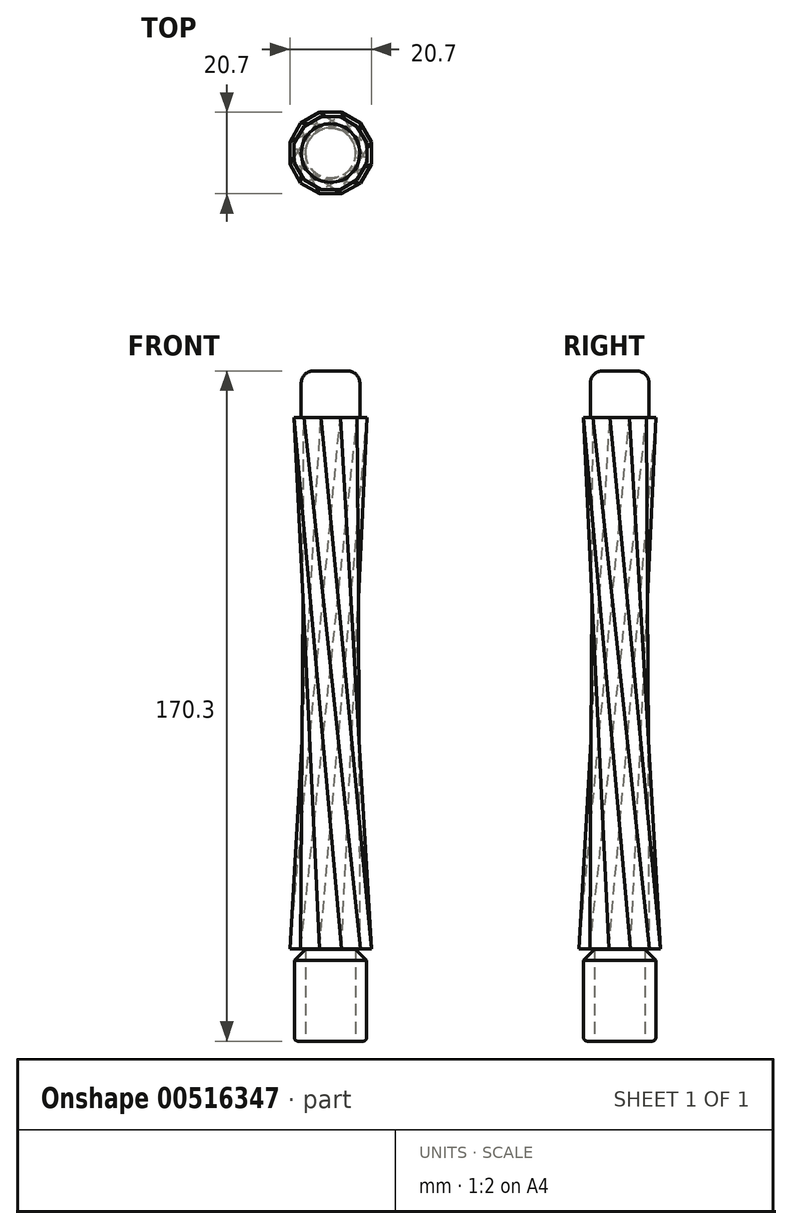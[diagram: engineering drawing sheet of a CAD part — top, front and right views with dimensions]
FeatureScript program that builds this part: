
annotation { "Feature Type Name" : "Feature", "Feature Type Description" : "" }
export const myFeature = defineFeature(function(context is Context, id is Id, definition is map)
    precondition{}
    {
        {
            var Q0;
            Q0=qCreatedBy(makeId("Top.planeOp"),FACE);
            cPlane(context, id + "F0", {"entities" : qUnion([Q0]), "cplaneType" : CPlaneType.OFFSET, "offset" : 2.5 * mm, "oppositeDirection" : true, "width" : 150 * mm, "height" : 150 * mm});
        }
        {
            var Q0;
            Q0=qCreatedBy(id+"F0.planeOp",FACE);
            var sketch = newSketch(context, id + "F1", { "sketchPlane" : qUnion([Q0])});
            skCircle(sketch, "E0", {"center": v(0, 0) * mm, "radius": 6.4 * mm});
            skCircle(sketch, "E1", {"center": v(0, 0) * mm, "radius": 9.2 * mm});
            skCircle(sketch, "E2", {"center": v(0, 0) * mm, "radius": 10.35 * mm});
            skSolve(sketch);
        }
        {
            var Q0;
            Q0=qCreatedBy(makeId("Top.planeOp"),FACE);
            cPlane(context, id + "F2", {"entities" : qUnion([Q0]), "cplaneType" : CPlaneType.OFFSET, "offset" : 21 * mm, "width" : 150 * mm, "height" : 150 * mm});
        }
        {
            var Q0;
            Q0=qCreatedBy(id+"F2.planeOp",FACE);
            var sketch = newSketch(context, id + "F3", { "sketchPlane" : qUnion([Q0])});
            skCircle(sketch, "E3", {"center": v(0, 0) * mm, "radius": 6.4 * mm});
            skCircle(sketch, "E4", {"center": v(0, 0) * mm, "radius": 9.2 * mm});
            skCircle(sketch, "E5", {"center": v(0, 0) * mm, "radius": 10.35 * mm});
            skSolve(sketch);
        }
        {
            var Q0;
            Q0=qCreatedBy(id+"F2.planeOp",FACE);
            cPlane(context, id + "F4", {"entities" : qUnion([Q0]), "cplaneType" : CPlaneType.OFFSET, "offset" : 135 * mm, "width" : 150 * mm, "height" : 150 * mm});
        }
        {
            var Q0;
            Q0=qCreatedBy(id+"F4.planeOp",FACE);
            var sketch = newSketch(context, id + "F5", { "sketchPlane" : qUnion([Q0])});
            skPoint(sketch, "E6.0", {"position": v(0, 0) * mm});
            skCircle(sketch, "E7", {"center": v(0, 0) * mm, "radius": 4.9 * mm});
            skCircle(sketch, "E8", {"center": v(0, 0) * mm, "radius": 7.45 * mm});
            skCircle(sketch, "E9", {"center": v(0, 0) * mm, "radius": 9.25 * mm});
            skSolve(sketch);
        }
        {
            var Q0;
            Q0=qCreatedBy(id+"F4.planeOp",FACE);
            cPlane(context, id + "F6", {"entities" : qUnion([Q0]), "cplaneType" : CPlaneType.OFFSET, "offset" : 11.8 * mm, "width" : 150 * mm, "height" : 150 * mm});
        }
        {
            var Q0;
            Q0=qCreatedBy(id+"F6.planeOp",FACE);
            var sketch = newSketch(context, id + "F7", { "sketchPlane" : qUnion([Q0])});
            skPoint(sketch, "E10.0", {"position": v(0, 0) * mm});
            skCircle(sketch, "E11", {"center": v(0, 0) * mm, "radius": 4.9 * mm});
            skCircle(sketch, "E12", {"center": v(0, 0) * mm, "radius": 7.45 * mm});
            skCircle(sketch, "E13", {"center": v(0, 0) * mm, "radius": 9.25 * mm});
            skSolve(sketch);
        }
        {
            var Q0;
            Q0=qCreatedBy(makeId("Front.planeOp"),FACE);
            var sketch = newSketch(context, id + "F8", { "sketchPlane" : qUnion([Q0])});
            skPoint(sketch, "E14.0", {"position": v(0, 167.8) * mm});
            skLineSegment(sketch, "E15", {"start": v(0, 167.8) * mm, "end": v(0, 0) * mm, "construction": true});
            skCircle(sketch, "E16", {"center": v(0, 36.85) * mm, "radius": 2.35 * mm});
            skCircle(sketch, "E17", {"center": v(0, 57.2) * mm, "radius": 2.6 * mm});
            skCircle(sketch, "E18", {"center": v(0, 79.25) * mm, "radius": 2.75 * mm});
            skCircle(sketch, "E19", {"center": v(0, 102.2) * mm, "radius": 2.3 * mm});
            skCircle(sketch, "E20", {"center": v(0, 127.6) * mm, "radius": 3 * mm});
            skCircle(sketch, "E21", {"center": v(2.3, 147.6) * mm, "radius": 2.1 * mm});
            skCircle(sketch, "E22", {"center": v(-3.01, 148.25) * mm, "radius": 1.45 * mm});
            skCircle(sketch, "E23", {"center": v(0, 30.75) * mm, "radius": 2.75 * mm});
            skSolve(sketch);
        }
        {
            var Q0;
            Q0=makeQuery(id+"F1.imprint","IMPRINT",FACE,{"disambiguationData":[TD([[makeQuery(id+"F1.imprint","IMPRINT",EDGE,{"derivedFrom":sQuery(id+"F1.wireOp",EDGE,"E0")}),1.0]])]});
            var Q1;
            Q1=makeQuery(id+"F3.imprint","IMPRINT",FACE,{"disambiguationData":[TD([[makeQuery(id+"F3.imprint","IMPRINT",EDGE,{"derivedFrom":sQuery(id+"F3.wireOp",EDGE,"E3")}),1.0]])]});
            var Q2;
            Q2=makeQuery(id+"F5.imprint","IMPRINT",FACE,{"disambiguationData":[TD([[makeQuery(id+"F5.imprint","IMPRINT",EDGE,{"derivedFrom":sQuery(id+"F5.wireOp",EDGE,"E7")}),1.0]])]});
            var Q3;
            Q3=makeQuery(id+"F7.imprint","IMPRINT",FACE,{"disambiguationData":[TD([[makeQuery(id+"F7.imprint","IMPRINT",EDGE,{"derivedFrom":sQuery(id+"F7.wireOp",EDGE,"E11")}),1.0]])]});
            loft(context, id + "F9", {"sheetProfilesArray" : [{ "sheetProfileEntities" : qUnion([Q0]) }, { "sheetProfileEntities" : qUnion([Q1]) }, { "sheetProfileEntities" : qUnion([Q2]) }, { "sheetProfileEntities" : qUnion([Q3]) }]});
        }
        {
            var Q0;
            Q0=makeQuery(id+"F8.imprint","IMPRINT",FACE,{"disambiguationData":[TD([[makeQuery(id+"F8.imprint","IMPRINT",EDGE,{"derivedFrom":sQuery(id+"F8.wireOp",EDGE,"E23")}),1.0]])]});
            extrude(context, id + "F10", {"entities" : qUnion([Q0]), "operationType" : NewBodyOperationType.ADD, "oppositeDirection" : true, "depth" : 15 * mm});
        }
        {
            var Q0;
            Q0=makeQuery(id+"F8.imprint","IMPRINT",FACE,{"disambiguationData":[TD([[makeQuery(id+"F8.imprint","IMPRINT",EDGE,{"derivedFrom":sQuery(id+"F8.wireOp",EDGE,"E16")}),1.0]])]});
            var Q1;
            Q1=makeQuery(id+"F8.imprint","IMPRINT",FACE,{"disambiguationData":[TD([[makeQuery(id+"F8.imprint","IMPRINT",EDGE,{"derivedFrom":sQuery(id+"F8.wireOp",EDGE,"E17")}),1.0]])]});
            var Q2;
            Q2=makeQuery(id+"F8.imprint","IMPRINT",FACE,{"disambiguationData":[TD([[makeQuery(id+"F8.imprint","IMPRINT",EDGE,{"derivedFrom":sQuery(id+"F8.wireOp",EDGE,"E18")}),1.0]])]});
            var Q3;
            Q3=makeQuery(id+"F8.imprint","IMPRINT",FACE,{"disambiguationData":[TD([[makeQuery(id+"F8.imprint","IMPRINT",EDGE,{"derivedFrom":sQuery(id+"F8.wireOp",EDGE,"E19")}),1.0]])]});
            var Q4;
            Q4=makeQuery(id+"F8.imprint","IMPRINT",FACE,{"disambiguationData":[TD([[makeQuery(id+"F8.imprint","IMPRINT",EDGE,{"derivedFrom":sQuery(id+"F8.wireOp",EDGE,"E20")}),1.0]])]});
            var Q5;
            Q5=makeQuery(id+"F8.imprint","IMPRINT",FACE,{"disambiguationData":[TD([[makeQuery(id+"F8.imprint","IMPRINT",EDGE,{"derivedFrom":sQuery(id+"F8.wireOp",EDGE,"E21")}),1.0]])]});
            var Q6;
            Q6=makeQuery(id+"F8.imprint","IMPRINT",FACE,{"disambiguationData":[TD([[makeQuery(id+"F8.imprint","IMPRINT",EDGE,{"derivedFrom":sQuery(id+"F8.wireOp",EDGE,"E22")}),1.0]])]});
            extrude(context, id + "F11", {"entities" : qUnion([Q0, Q1, Q2, Q3, Q4, Q5, Q6]), "operationType" : NewBodyOperationType.ADD, "depth" : 15 * mm});
        }
        {
            var Q0;
            Q0=makeQuery(id+"F1.imprint","IMPRINT",FACE,{"disambiguationData":[TD([[makeQuery(id+"F1.imprint","IMPRINT",EDGE,{"derivedFrom":sQuery(id+"F1.wireOp",EDGE,"E0")}),-1.0]])]});
            var Q1;
            Q1=makeQuery(id+"F1.imprint","IMPRINT",FACE,{"disambiguationData":[TD([[makeQuery(id+"F1.imprint","IMPRINT",EDGE,{"derivedFrom":sQuery(id+"F1.wireOp",EDGE,"E0")}),1.0]])]});
            extrude(context, id + "F12", {"entities" : qUnion([Q0, Q1]), "depth" : 23.5 * mm, "offsetDistance" : 25 * mm});
        }
        {
            var Q0;
            Q0=makeQuery(id+"F7.imprint","IMPRINT",FACE,{"disambiguationData":[TD([[makeQuery(id+"F7.imprint","IMPRINT",EDGE,{"derivedFrom":sQuery(id+"F7.wireOp",EDGE,"E11")}),-1.0]])]});
            var Q1;
            Q1=makeQuery(id+"F7.imprint","IMPRINT",FACE,{"disambiguationData":[TD([[makeQuery(id+"F7.imprint","IMPRINT",EDGE,{"derivedFrom":sQuery(id+"F7.wireOp",EDGE,"E11")}),1.0]])]});
            extrude(context, id + "F13", {"entities" : qUnion([Q0, Q1]), "oppositeDirection" : true, "depth" : 11.8 * mm, "offsetDistance" : 25 * mm});
        }
        {
            var Q0;
            Q0=qCreatedBy(id+"F2.planeOp",FACE);
            var sketch = newSketch(context, id + "F14", { "sketchPlane" : qUnion([Q0])});
            skPoint(sketch, "E24.0", {"position": v(0, 0) * mm});
            skLineSegment(sketch, "E25.0", {"start": v(-2.77, 10.35) * mm, "end": v(2.77, 10.35) * mm});
            skLineSegment(sketch, "E25.1", {"start": v(2.77, 10.35) * mm, "end": v(7.58, 7.58) * mm});
            skLineSegment(sketch, "E25.2", {"start": v(7.58, 7.58) * mm, "end": v(10.35, 2.77) * mm});
            skLineSegment(sketch, "E25.3", {"start": v(10.35, 2.77) * mm, "end": v(10.35, -2.77) * mm});
            skLineSegment(sketch, "E25.4", {"start": v(10.35, -2.77) * mm, "end": v(7.58, -7.58) * mm});
            skLineSegment(sketch, "E25.5", {"start": v(7.58, -7.58) * mm, "end": v(2.77, -10.35) * mm});
            skLineSegment(sketch, "E25.6", {"start": v(2.77, -10.35) * mm, "end": v(-2.77, -10.35) * mm});
            skLineSegment(sketch, "E25.7", {"start": v(-2.77, -10.35) * mm, "end": v(-7.58, -7.58) * mm});
            skLineSegment(sketch, "E25.8", {"start": v(-7.58, -7.58) * mm, "end": v(-10.35, -2.77) * mm});
            skLineSegment(sketch, "E25.9", {"start": v(-10.35, -2.77) * mm, "end": v(-10.35, 2.77) * mm});
            skLineSegment(sketch, "E25.10", {"start": v(-10.35, 2.77) * mm, "end": v(-7.58, 7.58) * mm});
            skLineSegment(sketch, "E25.11", {"start": v(-7.58, 7.58) * mm, "end": v(-2.77, 10.35) * mm});
            skPoint(sketch, "E25.0.midPoint", {"position": v(0, 10.35) * mm});
            skSolve(sketch);
        }
        {
            var Q0;
            Q0=qCreatedBy(id+"F4.planeOp",FACE);
            var sketch = newSketch(context, id + "F15", { "sketchPlane" : qUnion([Q0])});
            skPoint(sketch, "E26.0", {"position": v(0, 0) * mm});
            skLineSegment(sketch, "E27.0", {"start": v(-2.48, 9.25) * mm, "end": v(2.48, 9.25) * mm});
            skLineSegment(sketch, "E27.1", {"start": v(2.48, 9.25) * mm, "end": v(6.77, 6.77) * mm});
            skLineSegment(sketch, "E27.2", {"start": v(6.77, 6.77) * mm, "end": v(9.25, 2.48) * mm});
            skLineSegment(sketch, "E27.3", {"start": v(9.25, 2.48) * mm, "end": v(9.25, -2.48) * mm});
            skLineSegment(sketch, "E27.4", {"start": v(9.25, -2.48) * mm, "end": v(6.77, -6.77) * mm});
            skLineSegment(sketch, "E27.5", {"start": v(6.77, -6.77) * mm, "end": v(2.48, -9.25) * mm});
            skLineSegment(sketch, "E27.6", {"start": v(2.48, -9.25) * mm, "end": v(-2.48, -9.25) * mm});
            skLineSegment(sketch, "E27.7", {"start": v(-2.48, -9.25) * mm, "end": v(-6.77, -6.77) * mm});
            skLineSegment(sketch, "E27.8", {"start": v(-6.77, -6.77) * mm, "end": v(-9.25, -2.48) * mm});
            skLineSegment(sketch, "E27.9", {"start": v(-9.25, -2.48) * mm, "end": v(-9.25, 2.48) * mm});
            skLineSegment(sketch, "E27.10", {"start": v(-9.25, 2.48) * mm, "end": v(-6.77, 6.77) * mm});
            skLineSegment(sketch, "E27.11", {"start": v(-6.77, 6.77) * mm, "end": v(-2.48, 9.25) * mm});
            skPoint(sketch, "E27.0.midPoint", {"position": v(0, 9.25) * mm});
            skSolve(sketch);
        }
        {
            var Q0;
            Q0=makeQuery(id+"F14.imprint","IMPRINT",FACE,{"disambiguationData":[TD([[makeQuery(id+"F14.imprint","IMPRINT",EDGE,{"derivedFrom":sQuery(id+"F14.wireOp",EDGE,"E25.0")}),-1.0]])]});
            var Q1;
            Q1=makeQuery(id+"F15.imprint","IMPRINT",FACE,{"disambiguationData":[TD([[makeQuery(id+"F15.imprint","IMPRINT",EDGE,{"derivedFrom":sQuery(id+"F15.wireOp",EDGE,"E27.0")}),-1.0]])]});
            var Q2;
            Q2=sQuery(id+"F14.wireOp",VERTEX,"E25.6.start");
            var Q3;
            Q3=sQuery(id+"F15.wireOp",VERTEX,"E27.9.start");
            loft(context, id + "F16", {"sheetProfilesArray" : [{ "sheetProfileEntities" : qUnion([Q0]) }, { "sheetProfileEntities" : qUnion([Q1]) }], "matchConnections" : true, "connections" : [{ "connectionEntities" : qUnion([Q2, Q3]), "connectionEdgeQueries" : qUnion([]), "connectionEdgeParameters" : [] }]});
        }
        {
            var Q0;
            Q0=qCreatedBy(makeId("Right.planeOp"),FACE);
            var sketch = newSketch(context, id + "F17", { "sketchPlane" : qUnion([Q0])});
            skCircle(sketch, "E28", {"center": v(-17, 147.6) * mm, "radius": 10 * mm});
            skSolve(sketch);
        }
        {
            var Q0;
            Q0=makeQuery(id+"F17.imprint","IMPRINT",FACE,{"disambiguationData":[TD([[makeQuery(id+"F17.imprint","IMPRINT",EDGE,{"derivedFrom":sQuery(id+"F17.wireOp",EDGE,"E28")}),1.0]])]});
            extrude(context, id + "F18", {"entities" : qUnion([Q0]), "endBound" : BoundingType.SYMMETRIC, "oppositeDirection" : true, "depth" : 15 * mm});
        }
        {
            var Q0;
            Q0=makeQuery(id+"F12.opExtrude","CAP_EDGE",EDGE,{"disambiguationData":[OSD([sQuery(id+"F1.wireOp",EDGE,"E1")])],"isStart":true});
            fillet(context, id + "F19", {"entities" : qUnion([Q0]), "radius" : 1 * mm, "tangentPropagation" : true, "allowEdgeOverflow" : false});
        }
        {
            var Q0;
            Q0=makeQuery(id+"F13.opExtrude","CAP_EDGE",EDGE,{"disambiguationData":[OSD([sQuery(id+"F7.wireOp",EDGE,"E12")])],"isStart":true});
            fillet(context, id + "F20", {"entities" : qUnion([Q0]), "radius" : 3.1 * mm, "tangentPropagation" : true, "allowEdgeOverflow" : false});
        }
        {
            var Q0;
            Q0=makeQuery(id+"F9.opLoft","SWEPT_BODY",BODY,{"disambiguationData":[OSD([makeQuery(id+"F1.imprint","IMPRINT",FACE,{"disambiguationData":[TD([[makeQuery(id+"F1.imprint","IMPRINT",EDGE,{"derivedFrom":sQuery(id+"F1.wireOp",EDGE,"E0")}),1.0]])]}),sQuery(id+"F3.wireOp",EDGE,"E3"),sQuery(id+"F5.wireOp",EDGE,"E7"),makeQuery(id+"F7.imprint","IMPRINT",FACE,{"disambiguationData":[TD([[makeQuery(id+"F7.imprint","IMPRINT",EDGE,{"derivedFrom":sQuery(id+"F7.wireOp",EDGE,"E11")}),1.0]])]})])]});
            var Q1;
            Q1=makeQuery(id+"F12.opExtrude","SWEPT_BODY",BODY,{"disambiguationData":[OSD([sQuery(id+"F1.wireOp",EDGE,"E1")])]});
            booleanBodies(context, id + "F21", {"operationType" : BooleanOperationType.SUBTRACTION, "tools" : qUnion([Q0]), "targets" : qUnion([Q1])});
        }
        {
            var Q0;
            Q0=makeQuery(id+"F18.opExtrude","SWEPT_BODY",BODY,{"disambiguationData":[OSD([sQuery(id+"F17.wireOp",EDGE,"E28")])]});
            var Q1;
            Q1=makeQuery(id+"F12.opExtrude","SWEPT_BODY",BODY,{"disambiguationData":[OSD([sQuery(id+"F1.wireOp",EDGE,"E1")])]});
            booleanBodies(context, id + "F22", {"operationType" : BooleanOperationType.SUBTRACTION, "tools" : qUnion([Q0]), "targets" : qUnion([Q1])});
        }
        {
            var Q0;
            Q0=makeQuery(id+"F12.opExtrude","CAP_EDGE",EDGE,{"disambiguationData":[OSD([sQuery(id+"F1.wireOp",EDGE,"E1")])],"isStart":false});
            chamfer(context, id + "F23", {"entities" : qUnion([Q0]), "width" : 3 * mm, "tangentPropagation" : true});
        }
    });
